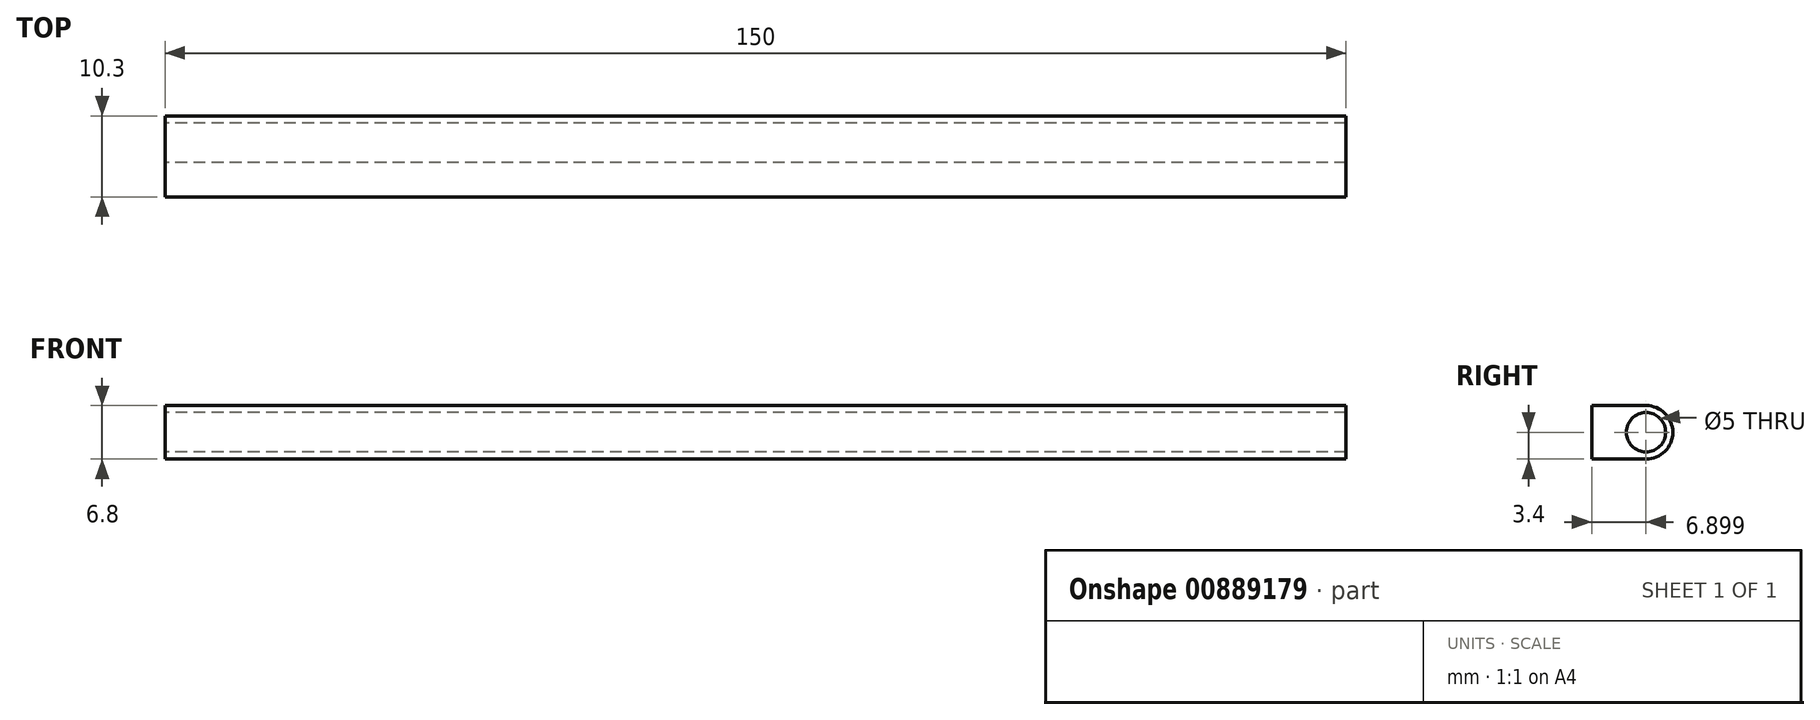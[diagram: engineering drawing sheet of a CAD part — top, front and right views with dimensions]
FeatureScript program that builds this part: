
annotation { "Feature Type Name" : "Feature", "Feature Type Description" : "" }
export const myFeature = defineFeature(function(context is Context, id is Id, definition is map)
    precondition{}
    {
        {
            var Q0;
            Q0=qCreatedBy(makeId("Top.planeOp"),FACE);
            var sketch = newSketch(context, id + "F0", { "sketchPlane" : qUnion([Q0])});
            skLineSegment(sketch, "E0.bottom", {"start": v(-27.68, 3.38) * mm, "end": v(122.32, 3.38) * mm});
            skLineSegment(sketch, "E0.top", {"start": v(-27.68, -6.92) * mm, "end": v(122.32, -6.92) * mm});
            skLineSegment(sketch, "E0.left", {"start": v(-27.68, 3.38) * mm, "end": v(-27.68, -6.92) * mm});
            skLineSegment(sketch, "E0.right", {"start": v(122.32, 3.38) * mm, "end": v(122.32, -6.92) * mm});
            skSolve(sketch);
        }
        {
            var Q0;
            Q0=makeQuery(id+"F0.imprint","IMPRINT",FACE,{"disambiguationData":[TD([[makeQuery(id+"F0.imprint","IMPRINT",EDGE,{"derivedFrom":sQuery(id+"F0.wireOp",EDGE,"E0.bottom")}),-1.0]])]});
            extrude(context, id + "F1", {"entities" : qUnion([Q0]), "depth" : 6.8 * mm, "offsetDistance" : 25 * mm});
        }
        {
            var Q0;
            Q0=makeQuery(id+"F1.opExtrude","CAP_EDGE",EDGE,{"disambiguationData":[OSD([sQuery(id+"F0.wireOp",EDGE,"E0.bottom")])],"isStart":false});
            var Q1;
            Q1=makeQuery(id+"F1.opExtrude","CAP_EDGE",EDGE,{"disambiguationData":[OSD([sQuery(id+"F0.wireOp",EDGE,"E0.bottom")])],"isStart":true});
            fillet(context, id + "F2", {"entities" : qUnion([Q0, Q1]), "radius" : 3.4 * mm, "tangentPropagation" : true, "allowEdgeOverflow" : false});
        }
        {
            var Q0;
            Q0=makeQuery(id+"F1.opExtrude","SWEPT_FACE",FACE,{"disambiguationData":[OSD([sQuery(id+"F0.wireOp",EDGE,"E0.left")])]});
            var sketch = newSketch(context, id + "F3", { "sketchPlane" : qUnion([Q0])});
            skPoint(sketch, "E1", {"position": v(0.02, 6.8) * mm});
            skPoint(sketch, "E2", {"position": v(0.02, 0) * mm});
            skPoint(sketch, "E3", {"position": v(0.02, 3.4) * mm});
            skCircle(sketch, "E4", {"center": v(0.02, 3.4) * mm, "radius": 2.5 * mm});
            skSolve(sketch);
        }
        {
            var Q0;
            Q0=makeQuery(id+"F3.imprint","IMPRINT",FACE,{"disambiguationData":[TD([[makeQuery(id+"F3.imprint","IMPRINT",EDGE,{"derivedFrom":sQuery(id+"F3.wireOp",EDGE,"E4")}),1.0]])]});
            extrude(context, id + "F4", {"entities" : qUnion([Q0]), "operationType" : NewBodyOperationType.REMOVE, "endBound" : BoundingType.THROUGH_ALL, "oppositeDirection" : true, "depth" : 25 * mm, "offsetDistance" : 25 * mm});
        }
    });
